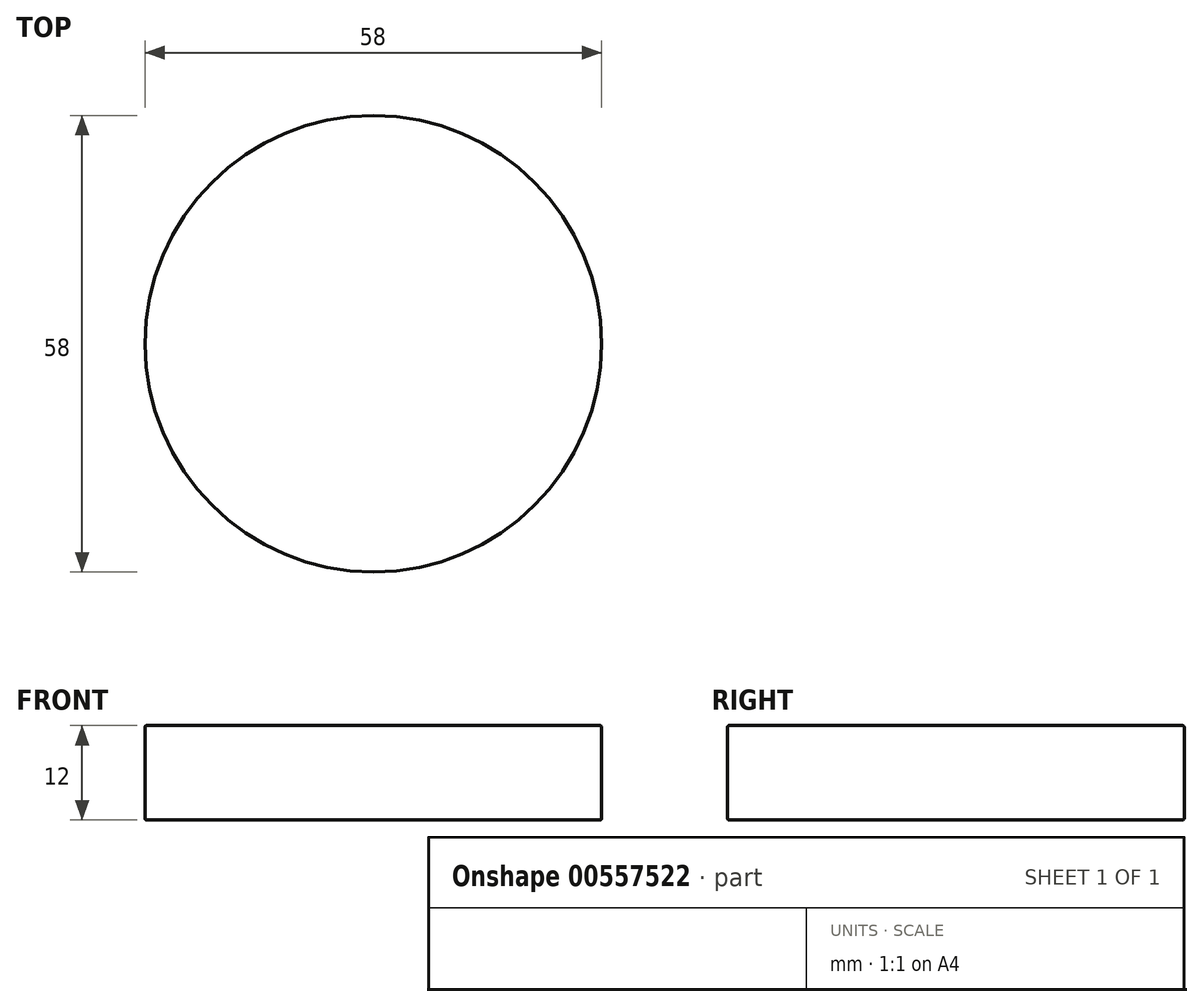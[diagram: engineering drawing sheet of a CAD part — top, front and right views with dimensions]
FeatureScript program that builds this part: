
annotation { "Feature Type Name" : "Feature", "Feature Type Description" : "" }
export const myFeature = defineFeature(function(context is Context, id is Id, definition is map)
    precondition{}
    {
        {
            var Q0;
            Q0=qCreatedBy(makeId("Top.planeOp"),FACE);
            var sketch = newSketch(context, id + "F0", { "sketchPlane" : qUnion([Q0])});
            skCircle(sketch, "E0", {"center": v(0, 0) * mm, "radius": 29 * mm});
            skSolve(sketch);
        }
        {
            var Q0;
            Q0=makeQuery(id+"F0.imprint","IMPRINT",FACE,{"disambiguationData":[TD([[makeQuery(id+"F0.imprint","IMPRINT",EDGE,{"derivedFrom":sQuery(id+"F0.wireOp",EDGE,"E0")}),1.0]])]});
            var Q1;
            Q1=sQuery(id+"F0.wireOp",EDGE,"E0");
            extrude(context, id + "F1", {"entities" : qUnion([Q0]), "surfaceEntities" : qUnion([Q1]), "depth" : 12 * mm, "offsetDistance" : 25 * mm});
        }
        {
            var Q0;
            Q0=makeQuery(id+"F1.opExtrude","CAP_EDGE",EDGE,{"disambiguationData":[OSD([sQuery(id+"F0.wireOp",EDGE,"E0")])],"isStart":false});
            var Q1;
            Q1=makeQuery(id+"F1.opExtrude","CAP_EDGE",EDGE,{"disambiguationData":[OSD([sQuery(id+"F0.wireOp",EDGE,"E0")])],"isStart":true});
            fillet(context, id + "F2", {"entities" : qUnion([Q0, Q1]), "radius" : 0.2 * mm, "allowEdgeOverflow" : false});
        }
    });
